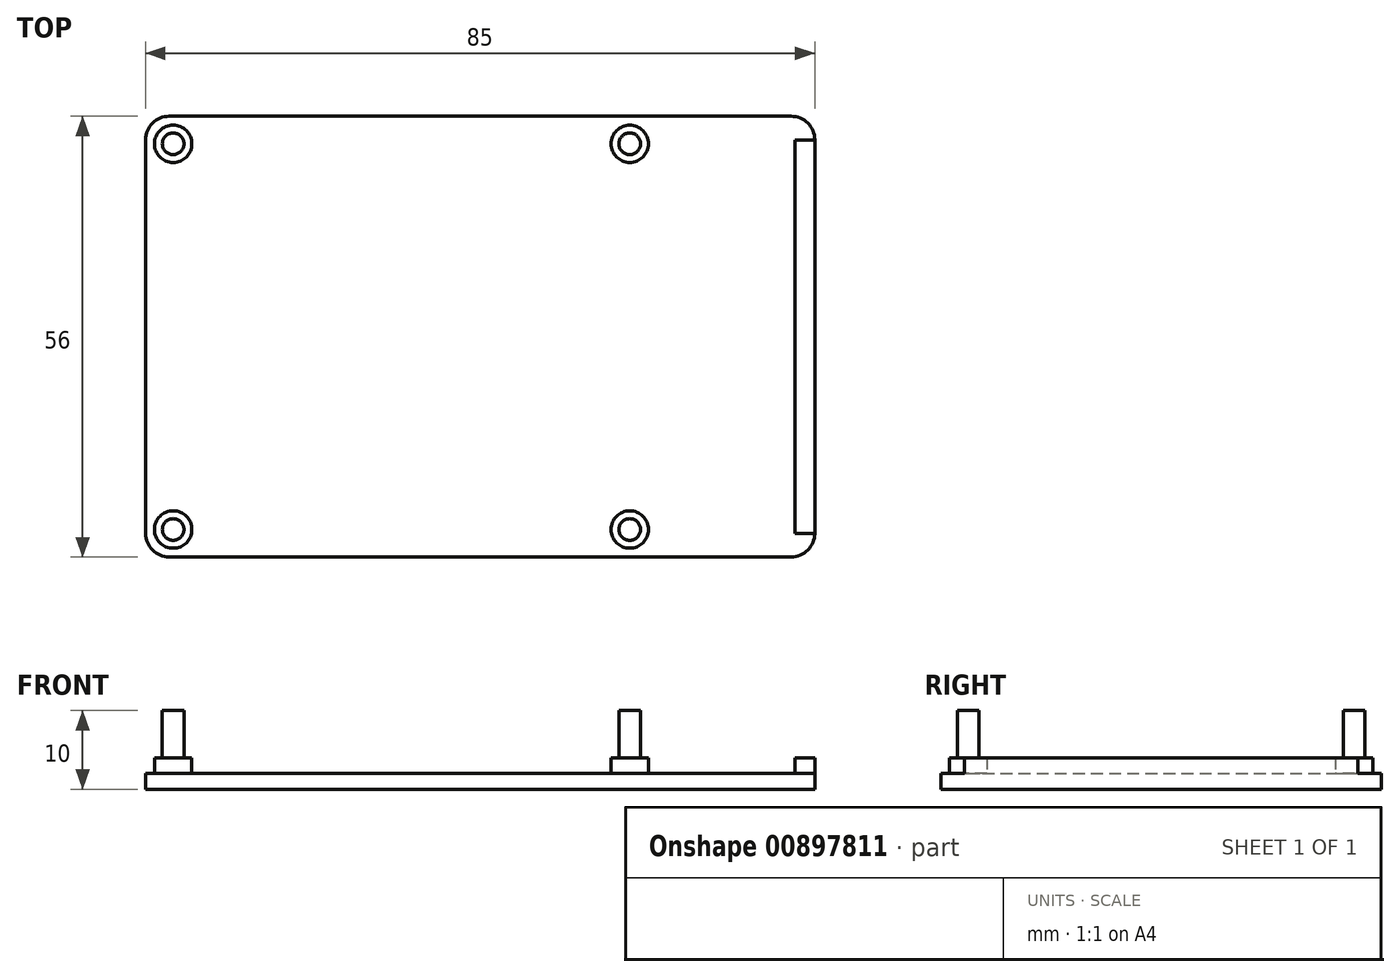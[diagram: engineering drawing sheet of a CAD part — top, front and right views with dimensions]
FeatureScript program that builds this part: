
annotation { "Feature Type Name" : "Feature", "Feature Type Description" : "" }
export const myFeature = defineFeature(function(context is Context, id is Id, definition is map)
    precondition{}
    {
        {
            var Q0;
            Q0=qCreatedBy(makeId("Top.planeOp"),FACE);
            var sketch = newSketch(context, id + "F0", { "sketchPlane" : qUnion([Q0])});
            skLineSegment(sketch, "E0.bottom", {"start": v(-29, 24.5) * mm, "end": v(29, 24.5) * mm});
            skLineSegment(sketch, "E0.top", {"start": v(-29, -24.5) * mm, "end": v(29, -24.5) * mm});
            skLineSegment(sketch, "E0.left", {"start": v(-29, 24.5) * mm, "end": v(-29, -24.5) * mm});
            skLineSegment(sketch, "E0.right", {"start": v(29, 24.5) * mm, "end": v(29, -24.5) * mm});
            skPoint(sketch, "E0.middle", {"position": v(0, 0) * mm});
            skLineSegment(sketch, "E1.top", {"start": v(-29.5, -28) * mm, "end": v(-29.07, -28) * mm});
            skLineSegment(sketch, "E1.left", {"start": v(-32.5, -24.5) * mm, "end": v(-32.5, -25) * mm});
            skLineSegment(sketch, "E2.bottom", {"start": v(-29.5, -28) * mm, "end": v(49.5, -28) * mm});
            skLineSegment(sketch, "E2.top", {"start": v(-29.5, 28) * mm, "end": v(49.5, 28) * mm});
            skLineSegment(sketch, "E2.left", {"start": v(-32.5, -25) * mm, "end": v(-32.5, 25) * mm});
            skLineSegment(sketch, "E2.right", {"start": v(52.5, -25) * mm, "end": v(52.5, 25) * mm});
            skPoint(sketch, "E3.visualSharp", {"position": v(-32.5, 28) * mm});
            skArc(sketch, "E3.filletArc", {"start": v(-29.5, 28) * mm, "mid": v(-31.62, 27.12) * mm, "end": v(-32.5, 25) * mm});
            skPoint(sketch, "E4.visualSharp", {"position": v(-32.5, -28) * mm});
            skArc(sketch, "E4.filletArc", {"start": v(-32.5, -25) * mm, "mid": v(-31.62, -27.12) * mm, "end": v(-29.5, -28) * mm});
            skPoint(sketch, "E5.visualSharp", {"position": v(52.5, -28) * mm});
            skArc(sketch, "E5.filletArc", {"start": v(49.5, -28) * mm, "mid": v(51.62, -27.12) * mm, "end": v(52.5, -25) * mm});
            skPoint(sketch, "E6.visualSharp", {"position": v(52.5, 28) * mm});
            skArc(sketch, "E6.filletArc", {"start": v(52.5, 25) * mm, "mid": v(51.62, 27.12) * mm, "end": v(49.5, 28) * mm});
            skCircle(sketch, "E7", {"center": v(29, 24.5) * mm, "radius": 1.38 * mm});
            skCircle(sketch, "E8", {"center": v(29, -24.5) * mm, "radius": 1.38 * mm});
            skCircle(sketch, "E9", {"center": v(-29, -24.5) * mm, "radius": 1.38 * mm});
            skCircle(sketch, "E10", {"center": v(-29, 24.5) * mm, "radius": 1.38 * mm});
            skCircle(sketch, "E11.0", {"center": v(29, 24.5) * mm, "radius": 2.38 * mm});
            skCircle(sketch, "E12.0", {"center": v(29, -24.5) * mm, "radius": 2.38 * mm});
            skCircle(sketch, "E13.0", {"center": v(-29, -24.5) * mm, "radius": 2.38 * mm});
            skCircle(sketch, "E14.0", {"center": v(-29, 24.5) * mm, "radius": 2.38 * mm});
            skLineSegment(sketch, "E15.bottom", {"start": v(52.5, 25) * mm, "end": v(50, 25) * mm});
            skLineSegment(sketch, "E15.top", {"start": v(52.5, -25) * mm, "end": v(50, -25) * mm});
            skLineSegment(sketch, "E15.left", {"start": v(52.5, 25) * mm, "end": v(52.5, -25) * mm});
            skLineSegment(sketch, "E15.right", {"start": v(50, 25) * mm, "end": v(50, -25) * mm});
            skSolve(sketch);
        }
        {
            var Q0;
            Q0=makeQuery(id+"F0.imprint","IMPRINT",FACE,{"disambiguationData":[TD([[makeQuery(id+"F0.imprint","IMPRINT",EDGE,{"derivedFrom":sQuery(id+"F0.wireOp",EDGE,"E2.top")}),-1.0]])]});
            var Q1;
            {var subQ10=sQuery(id+"F0.wireOp",EDGE,"E14.0");var subQ13=sQuery(id+"F0.wireOp",EDGE,"E0.bottom");var subQ14=makeQuery(id+"F0.imprint","INTERSECT",VERTEX,{"derivedFrom":[subQ13,subQ10]});Q1=makeQuery(id+"F0.imprint","IMPRINT",FACE,{"disambiguationData":[TD([[makeQuery(id+"F0.imprint","IMPRINT",EDGE,{"disambiguationData":[TD([[subQ14,-1.0]])],"derivedFrom":subQ13}),-1.0]])]});}
            var Q2;
            {var subQ0=sQuery(id+"F0.wireOp",EDGE,"E0.left");var subQ1=sQuery(id+"F0.wireOp",EDGE,"E0.bottom");var subQ2=makeQuery(id+"F0.imprint","INTERSECT",VERTEX,{"derivedFrom":[subQ1,subQ0]});Q2=makeQuery(id+"F0.imprint","IMPRINT",FACE,{"disambiguationData":[TD([[makeQuery(id+"F0.imprint","IMPRINT",EDGE,{"disambiguationData":[TD([[subQ2,-1.0]])],"derivedFrom":subQ1}),1.0]])]});}
            var Q3;
            {var subQ0=sQuery(id+"F0.wireOp",EDGE,"E10");var subQ1=sQuery(id+"F0.wireOp",EDGE,"E0.bottom");var subQ2=makeQuery(id+"F0.imprint","INTERSECT",VERTEX,{"derivedFrom":[subQ1,subQ0]});Q3=makeQuery(id+"F0.imprint","IMPRINT",FACE,{"disambiguationData":[TD([[makeQuery(id+"F0.imprint","IMPRINT",EDGE,{"disambiguationData":[TD([[subQ2,-1.0]])],"derivedFrom":subQ1}),1.0]])]});}
            var Q4;
            {var subQ0=sQuery(id+"F0.wireOp",EDGE,"E0.left");var subQ1=sQuery(id+"F0.wireOp",EDGE,"E0.bottom");var subQ2=makeQuery(id+"F0.imprint","INTERSECT",VERTEX,{"derivedFrom":[subQ1,subQ0]});Q4=makeQuery(id+"F0.imprint","IMPRINT",FACE,{"disambiguationData":[TD([[makeQuery(id+"F0.imprint","IMPRINT",EDGE,{"disambiguationData":[TD([[subQ2,-1.0]])],"derivedFrom":subQ1}),-1.0]])]});}
            var Q5;
            {var subQ0=sQuery(id+"F0.wireOp",EDGE,"E10");var subQ1=sQuery(id+"F0.wireOp",EDGE,"E0.bottom");var subQ2=makeQuery(id+"F0.imprint","INTERSECT",VERTEX,{"derivedFrom":[subQ1,subQ0]});Q5=makeQuery(id+"F0.imprint","IMPRINT",FACE,{"disambiguationData":[TD([[makeQuery(id+"F0.imprint","IMPRINT",EDGE,{"disambiguationData":[TD([[subQ2,-1.0]])],"derivedFrom":subQ1}),-1.0]])]});}
            var Q6;
            {var subQ0=sQuery(id+"F0.wireOp",EDGE,"E0.left");var subQ1=sQuery(id+"F0.wireOp",EDGE,"E0.top");var subQ2=makeQuery(id+"F0.imprint","INTERSECT",VERTEX,{"derivedFrom":[subQ1,subQ0]});Q6=makeQuery(id+"F0.imprint","IMPRINT",FACE,{"disambiguationData":[TD([[makeQuery(id+"F0.imprint","IMPRINT",EDGE,{"disambiguationData":[TD([[subQ2,-1.0]])],"derivedFrom":subQ1}),-1.0]])]});}
            var Q7;
            {var subQ0=sQuery(id+"F0.wireOp",EDGE,"E9");var subQ1=sQuery(id+"F0.wireOp",EDGE,"E0.top");var subQ2=makeQuery(id+"F0.imprint","INTERSECT",VERTEX,{"derivedFrom":[subQ1,subQ0]});Q7=makeQuery(id+"F0.imprint","IMPRINT",FACE,{"disambiguationData":[TD([[makeQuery(id+"F0.imprint","IMPRINT",EDGE,{"disambiguationData":[TD([[subQ2,-1.0]])],"derivedFrom":subQ1}),-1.0]])]});}
            var Q8;
            {var subQ0=sQuery(id+"F0.wireOp",EDGE,"E0.left");var subQ1=sQuery(id+"F0.wireOp",EDGE,"E0.top");var subQ2=makeQuery(id+"F0.imprint","INTERSECT",VERTEX,{"derivedFrom":[subQ1,subQ0]});Q8=makeQuery(id+"F0.imprint","IMPRINT",FACE,{"disambiguationData":[TD([[makeQuery(id+"F0.imprint","IMPRINT",EDGE,{"disambiguationData":[TD([[subQ2,-1.0]])],"derivedFrom":subQ1}),1.0]])]});}
            var Q9;
            {var subQ0=sQuery(id+"F0.wireOp",EDGE,"E9");var subQ1=sQuery(id+"F0.wireOp",EDGE,"E0.top");var subQ2=makeQuery(id+"F0.imprint","INTERSECT",VERTEX,{"derivedFrom":[subQ1,subQ0]});Q9=makeQuery(id+"F0.imprint","IMPRINT",FACE,{"disambiguationData":[TD([[makeQuery(id+"F0.imprint","IMPRINT",EDGE,{"disambiguationData":[TD([[subQ2,-1.0]])],"derivedFrom":subQ1}),1.0]])]});}
            var Q10;
            {var subQ0=sQuery(id+"F0.wireOp",EDGE,"E12.0");var subQ1=sQuery(id+"F0.wireOp",EDGE,"E0.top");var subQ2=makeQuery(id+"F0.imprint","INTERSECT",VERTEX,{"derivedFrom":[subQ1,subQ0]});Q10=makeQuery(id+"F0.imprint","IMPRINT",FACE,{"disambiguationData":[TD([[makeQuery(id+"F0.imprint","IMPRINT",EDGE,{"disambiguationData":[TD([[subQ2,-1.0]])],"derivedFrom":subQ1}),1.0]])]});}
            var Q11;
            {var subQ0=sQuery(id+"F0.wireOp",EDGE,"E0.right");var subQ1=sQuery(id+"F0.wireOp",EDGE,"E0.top");var subQ2=makeQuery(id+"F0.imprint","INTERSECT",VERTEX,{"derivedFrom":[subQ1,subQ0]});Q11=makeQuery(id+"F0.imprint","IMPRINT",FACE,{"disambiguationData":[TD([[makeQuery(id+"F0.imprint","IMPRINT",EDGE,{"disambiguationData":[TD([[subQ2,1.0]])],"derivedFrom":subQ1}),1.0]])]});}
            var Q12;
            {var subQ0=sQuery(id+"F0.wireOp",EDGE,"E12.0");var subQ1=sQuery(id+"F0.wireOp",EDGE,"E0.top");var subQ2=makeQuery(id+"F0.imprint","INTERSECT",VERTEX,{"derivedFrom":[subQ1,subQ0]});Q12=makeQuery(id+"F0.imprint","IMPRINT",FACE,{"disambiguationData":[TD([[makeQuery(id+"F0.imprint","IMPRINT",EDGE,{"disambiguationData":[TD([[subQ2,-1.0]])],"derivedFrom":subQ1}),-1.0]])]});}
            var Q13;
            {var subQ0=sQuery(id+"F0.wireOp",EDGE,"E0.right");var subQ1=sQuery(id+"F0.wireOp",EDGE,"E0.top");var subQ2=makeQuery(id+"F0.imprint","INTERSECT",VERTEX,{"derivedFrom":[subQ1,subQ0]});Q13=makeQuery(id+"F0.imprint","IMPRINT",FACE,{"disambiguationData":[TD([[makeQuery(id+"F0.imprint","IMPRINT",EDGE,{"disambiguationData":[TD([[subQ2,1.0]])],"derivedFrom":subQ1}),-1.0]])]});}
            var Q14;
            {var subQ0=sQuery(id+"F0.wireOp",EDGE,"E11.0");var subQ1=sQuery(id+"F0.wireOp",EDGE,"E0.bottom");var subQ2=makeQuery(id+"F0.imprint","INTERSECT",VERTEX,{"derivedFrom":[subQ1,subQ0]});Q14=makeQuery(id+"F0.imprint","IMPRINT",FACE,{"disambiguationData":[TD([[makeQuery(id+"F0.imprint","IMPRINT",EDGE,{"disambiguationData":[TD([[subQ2,-1.0]])],"derivedFrom":subQ1}),1.0]])]});}
            var Q15;
            {var subQ0=sQuery(id+"F0.wireOp",EDGE,"E0.right");var subQ1=sQuery(id+"F0.wireOp",EDGE,"E0.bottom");var subQ2=makeQuery(id+"F0.imprint","INTERSECT",VERTEX,{"derivedFrom":[subQ1,subQ0]});Q15=makeQuery(id+"F0.imprint","IMPRINT",FACE,{"disambiguationData":[TD([[makeQuery(id+"F0.imprint","IMPRINT",EDGE,{"disambiguationData":[TD([[subQ2,1.0]])],"derivedFrom":subQ1}),1.0]])]});}
            var Q16;
            {var subQ0=sQuery(id+"F0.wireOp",EDGE,"E0.right");var subQ1=sQuery(id+"F0.wireOp",EDGE,"E0.bottom");var subQ2=makeQuery(id+"F0.imprint","INTERSECT",VERTEX,{"derivedFrom":[subQ1,subQ0]});Q16=makeQuery(id+"F0.imprint","IMPRINT",FACE,{"disambiguationData":[TD([[makeQuery(id+"F0.imprint","IMPRINT",EDGE,{"disambiguationData":[TD([[subQ2,1.0]])],"derivedFrom":subQ1}),-1.0]])]});}
            var Q17;
            {var subQ0=sQuery(id+"F0.wireOp",EDGE,"E11.0");var subQ1=sQuery(id+"F0.wireOp",EDGE,"E0.bottom");var subQ2=makeQuery(id+"F0.imprint","INTERSECT",VERTEX,{"derivedFrom":[subQ1,subQ0]});Q17=makeQuery(id+"F0.imprint","IMPRINT",FACE,{"disambiguationData":[TD([[makeQuery(id+"F0.imprint","IMPRINT",EDGE,{"disambiguationData":[TD([[subQ2,-1.0]])],"derivedFrom":subQ1}),-1.0]])]});}
            var Q18;
            Q18=makeQuery(id+"F0.imprint","IMPRINT",FACE,{"disambiguationData":[TD([[makeQuery(id+"F0.imprint","IMPRINT",EDGE,{"derivedFrom":sQuery(id+"F0.wireOp",EDGE,"E15.bottom")}),1.0]])]});
            extrude(context, id + "F1", {"entities" : qUnion([Q0, Q1, Q2, Q3, Q4, Q5, Q6, Q7, Q8, Q9, Q10, Q11, Q12, Q13, Q14, Q15, Q16, Q17, Q18]), "depth" : 2 * mm, "offsetDistance" : 25 * mm});
        }
        {
            var Q0;
            Q0=makeQuery(id+"F0.imprint","IMPRINT",FACE,{"disambiguationData":[TD([[makeQuery(id+"F0.imprint","IMPRINT",EDGE,{"derivedFrom":sQuery(id+"F0.wireOp",EDGE,"E15.bottom")}),1.0]])]});
            extrude(context, id + "F2", {"entities" : qUnion([Q0]), "operationType" : NewBodyOperationType.ADD, "depth" : 4 * mm, "offsetDistance" : 25 * mm});
        }
        {
            var Q0;
            {var subQ0=sQuery(id+"F0.wireOp",EDGE,"E9");var subQ1=sQuery(id+"F0.wireOp",EDGE,"E0.top");var subQ2=makeQuery(id+"F0.imprint","INTERSECT",VERTEX,{"derivedFrom":[subQ1,subQ0]});Q0=makeQuery(id+"F0.imprint","IMPRINT",FACE,{"disambiguationData":[TD([[makeQuery(id+"F0.imprint","IMPRINT",EDGE,{"disambiguationData":[TD([[subQ2,-1.0]])],"derivedFrom":subQ1}),-1.0]])]});}
            var Q1;
            {var subQ0=sQuery(id+"F0.wireOp",EDGE,"E9");var subQ1=sQuery(id+"F0.wireOp",EDGE,"E0.top");var subQ2=makeQuery(id+"F0.imprint","INTERSECT",VERTEX,{"derivedFrom":[subQ1,subQ0]});Q1=makeQuery(id+"F0.imprint","IMPRINT",FACE,{"disambiguationData":[TD([[makeQuery(id+"F0.imprint","IMPRINT",EDGE,{"disambiguationData":[TD([[subQ2,-1.0]])],"derivedFrom":subQ1}),1.0]])]});}
            var Q2;
            {var subQ0=sQuery(id+"F0.wireOp",EDGE,"E12.0");var subQ1=sQuery(id+"F0.wireOp",EDGE,"E0.top");var subQ2=makeQuery(id+"F0.imprint","INTERSECT",VERTEX,{"derivedFrom":[subQ1,subQ0]});Q2=makeQuery(id+"F0.imprint","IMPRINT",FACE,{"disambiguationData":[TD([[makeQuery(id+"F0.imprint","IMPRINT",EDGE,{"disambiguationData":[TD([[subQ2,-1.0]])],"derivedFrom":subQ1}),1.0]])]});}
            var Q3;
            {var subQ0=sQuery(id+"F0.wireOp",EDGE,"E12.0");var subQ1=sQuery(id+"F0.wireOp",EDGE,"E0.top");var subQ2=makeQuery(id+"F0.imprint","INTERSECT",VERTEX,{"derivedFrom":[subQ1,subQ0]});Q3=makeQuery(id+"F0.imprint","IMPRINT",FACE,{"disambiguationData":[TD([[makeQuery(id+"F0.imprint","IMPRINT",EDGE,{"disambiguationData":[TD([[subQ2,-1.0]])],"derivedFrom":subQ1}),-1.0]])]});}
            var Q4;
            {var subQ0=sQuery(id+"F0.wireOp",EDGE,"E11.0");var subQ1=sQuery(id+"F0.wireOp",EDGE,"E0.bottom");var subQ2=makeQuery(id+"F0.imprint","INTERSECT",VERTEX,{"derivedFrom":[subQ1,subQ0]});Q4=makeQuery(id+"F0.imprint","IMPRINT",FACE,{"disambiguationData":[TD([[makeQuery(id+"F0.imprint","IMPRINT",EDGE,{"disambiguationData":[TD([[subQ2,-1.0]])],"derivedFrom":subQ1}),1.0]])]});}
            var Q5;
            {var subQ0=sQuery(id+"F0.wireOp",EDGE,"E11.0");var subQ1=sQuery(id+"F0.wireOp",EDGE,"E0.bottom");var subQ2=makeQuery(id+"F0.imprint","INTERSECT",VERTEX,{"derivedFrom":[subQ1,subQ0]});Q5=makeQuery(id+"F0.imprint","IMPRINT",FACE,{"disambiguationData":[TD([[makeQuery(id+"F0.imprint","IMPRINT",EDGE,{"disambiguationData":[TD([[subQ2,-1.0]])],"derivedFrom":subQ1}),-1.0]])]});}
            var Q6;
            {var subQ0=sQuery(id+"F0.wireOp",EDGE,"E10");var subQ1=sQuery(id+"F0.wireOp",EDGE,"E0.bottom");var subQ2=makeQuery(id+"F0.imprint","INTERSECT",VERTEX,{"derivedFrom":[subQ1,subQ0]});Q6=makeQuery(id+"F0.imprint","IMPRINT",FACE,{"disambiguationData":[TD([[makeQuery(id+"F0.imprint","IMPRINT",EDGE,{"disambiguationData":[TD([[subQ2,-1.0]])],"derivedFrom":subQ1}),1.0]])]});}
            var Q7;
            {var subQ0=sQuery(id+"F0.wireOp",EDGE,"E10");var subQ1=sQuery(id+"F0.wireOp",EDGE,"E0.bottom");var subQ2=makeQuery(id+"F0.imprint","INTERSECT",VERTEX,{"derivedFrom":[subQ1,subQ0]});Q7=makeQuery(id+"F0.imprint","IMPRINT",FACE,{"disambiguationData":[TD([[makeQuery(id+"F0.imprint","IMPRINT",EDGE,{"disambiguationData":[TD([[subQ2,-1.0]])],"derivedFrom":subQ1}),-1.0]])]});}
            extrude(context, id + "F3", {"entities" : qUnion([Q0, Q1, Q2, Q3, Q4, Q5, Q6, Q7]), "operationType" : NewBodyOperationType.ADD, "depth" : 4 * mm, "offsetDistance" : 25 * mm});
        }
        {
            var Q0;
            {var subQ0=sQuery(id+"F0.wireOp",EDGE,"E0.right");var subQ1=sQuery(id+"F0.wireOp",EDGE,"E0.top");var subQ2=makeQuery(id+"F0.imprint","INTERSECT",VERTEX,{"derivedFrom":[subQ1,subQ0]});Q0=makeQuery(id+"F0.imprint","IMPRINT",FACE,{"disambiguationData":[TD([[makeQuery(id+"F0.imprint","IMPRINT",EDGE,{"disambiguationData":[TD([[subQ2,1.0]])],"derivedFrom":subQ1}),-1.0]])]});}
            var Q1;
            {var subQ0=sQuery(id+"F0.wireOp",EDGE,"E0.right");var subQ1=sQuery(id+"F0.wireOp",EDGE,"E0.top");var subQ2=makeQuery(id+"F0.imprint","INTERSECT",VERTEX,{"derivedFrom":[subQ1,subQ0]});Q1=makeQuery(id+"F0.imprint","IMPRINT",FACE,{"disambiguationData":[TD([[makeQuery(id+"F0.imprint","IMPRINT",EDGE,{"disambiguationData":[TD([[subQ2,1.0]])],"derivedFrom":subQ1}),1.0]])]});}
            var Q2;
            {var subQ0=sQuery(id+"F0.wireOp",EDGE,"E0.left");var subQ1=sQuery(id+"F0.wireOp",EDGE,"E0.top");var subQ2=makeQuery(id+"F0.imprint","INTERSECT",VERTEX,{"derivedFrom":[subQ1,subQ0]});Q2=makeQuery(id+"F0.imprint","IMPRINT",FACE,{"disambiguationData":[TD([[makeQuery(id+"F0.imprint","IMPRINT",EDGE,{"disambiguationData":[TD([[subQ2,-1.0]])],"derivedFrom":subQ1}),-1.0]])]});}
            var Q3;
            {var subQ0=sQuery(id+"F0.wireOp",EDGE,"E0.left");var subQ1=sQuery(id+"F0.wireOp",EDGE,"E0.top");var subQ2=makeQuery(id+"F0.imprint","INTERSECT",VERTEX,{"derivedFrom":[subQ1,subQ0]});Q3=makeQuery(id+"F0.imprint","IMPRINT",FACE,{"disambiguationData":[TD([[makeQuery(id+"F0.imprint","IMPRINT",EDGE,{"disambiguationData":[TD([[subQ2,-1.0]])],"derivedFrom":subQ1}),1.0]])]});}
            var Q4;
            {var subQ0=sQuery(id+"F0.wireOp",EDGE,"E0.left");var subQ1=sQuery(id+"F0.wireOp",EDGE,"E0.bottom");var subQ2=makeQuery(id+"F0.imprint","INTERSECT",VERTEX,{"derivedFrom":[subQ1,subQ0]});Q4=makeQuery(id+"F0.imprint","IMPRINT",FACE,{"disambiguationData":[TD([[makeQuery(id+"F0.imprint","IMPRINT",EDGE,{"disambiguationData":[TD([[subQ2,-1.0]])],"derivedFrom":subQ1}),1.0]])]});}
            var Q5;
            {var subQ0=sQuery(id+"F0.wireOp",EDGE,"E0.left");var subQ1=sQuery(id+"F0.wireOp",EDGE,"E0.bottom");var subQ2=makeQuery(id+"F0.imprint","INTERSECT",VERTEX,{"derivedFrom":[subQ1,subQ0]});Q5=makeQuery(id+"F0.imprint","IMPRINT",FACE,{"disambiguationData":[TD([[makeQuery(id+"F0.imprint","IMPRINT",EDGE,{"disambiguationData":[TD([[subQ2,-1.0]])],"derivedFrom":subQ1}),-1.0]])]});}
            var Q6;
            {var subQ0=sQuery(id+"F0.wireOp",EDGE,"E0.right");var subQ1=sQuery(id+"F0.wireOp",EDGE,"E0.bottom");var subQ2=makeQuery(id+"F0.imprint","INTERSECT",VERTEX,{"derivedFrom":[subQ1,subQ0]});Q6=makeQuery(id+"F0.imprint","IMPRINT",FACE,{"disambiguationData":[TD([[makeQuery(id+"F0.imprint","IMPRINT",EDGE,{"disambiguationData":[TD([[subQ2,1.0]])],"derivedFrom":subQ1}),1.0]])]});}
            var Q7;
            {var subQ0=sQuery(id+"F0.wireOp",EDGE,"E0.right");var subQ1=sQuery(id+"F0.wireOp",EDGE,"E0.bottom");var subQ2=makeQuery(id+"F0.imprint","INTERSECT",VERTEX,{"derivedFrom":[subQ1,subQ0]});Q7=makeQuery(id+"F0.imprint","IMPRINT",FACE,{"disambiguationData":[TD([[makeQuery(id+"F0.imprint","IMPRINT",EDGE,{"disambiguationData":[TD([[subQ2,1.0]])],"derivedFrom":subQ1}),-1.0]])]});}
            extrude(context, id + "F4", {"entities" : qUnion([Q0, Q1, Q2, Q3, Q4, Q5, Q6, Q7]), "operationType" : NewBodyOperationType.ADD, "depth" : 10 * mm, "offsetDistance" : 25 * mm});
        }
    });
